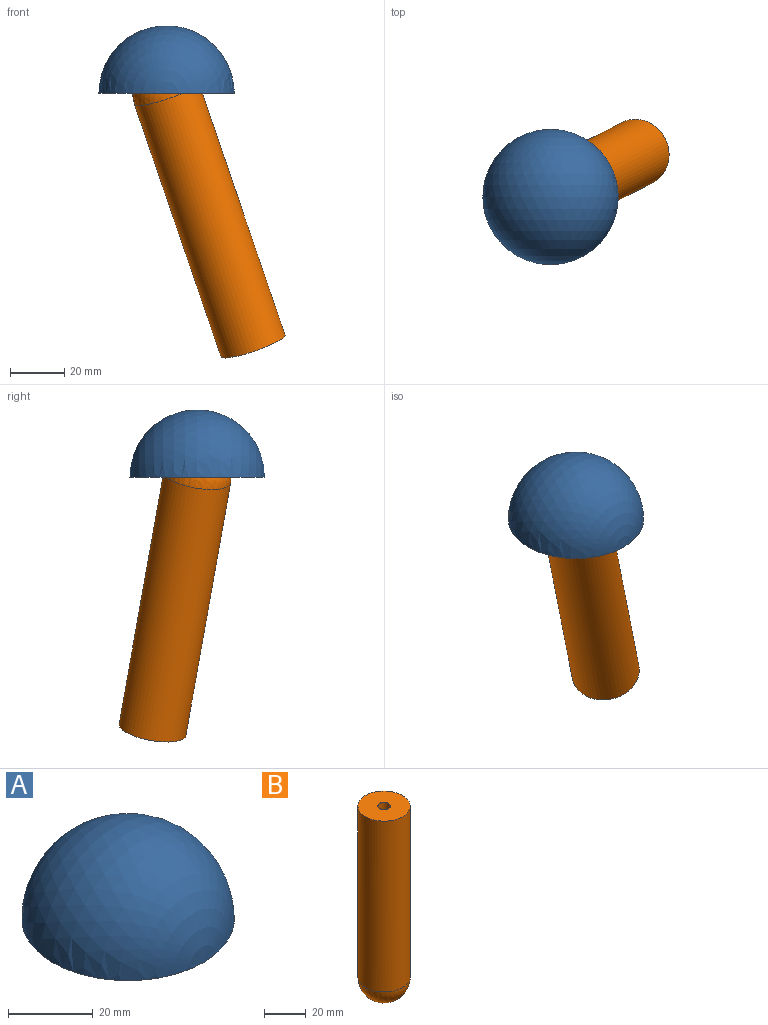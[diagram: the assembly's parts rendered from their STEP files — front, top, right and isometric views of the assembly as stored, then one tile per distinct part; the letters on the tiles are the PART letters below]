
ASSEMBLY  parts=2 mates=1
PART A: 3 faces, bbox 50x50x25 mm
  f0: sphere r=25mm, area 3927mm2, adj f2
  f1: sphere r=12.5mm, area 981.7mm2, adj f2
  f2: plane 50x50mm, normal (0,0,-1), area 1472.6mm2, adj f0,f1
PART B: 6 faces, bbox 25x25x112.5 mm
  f0: sphere r=12.5mm, area 28.7mm2, adj f1
  f1: cylinder r=3mm len=87.87mm, axis (0,0,-1), area 1656.2mm2, adj f0,f3
  f2: cylinder r=12.5mm len=100mm, axis (0,0,-1), area 7854mm2, adj f3,f4
  f3: plane 25x25mm, normal (0,0,1), area 462.6mm2, adj f1,f2
  f4: sphere r=12.5mm, area 981.7mm2, adj f2
  f5: sphere r=3mm, area 113.1mm2
PLACE A t=(73.26,-33.51,-21.59)mm fixed
PLACE B rot(axis=(-0.99,0.02,-0.16),170.1deg) t=(73.26,-33.51,-21.59)mm
MATE ball B.f1 <-> A.f2  axis (0.32,0.17,-0.93) through (73.26,-33.51,-21.59)mm
